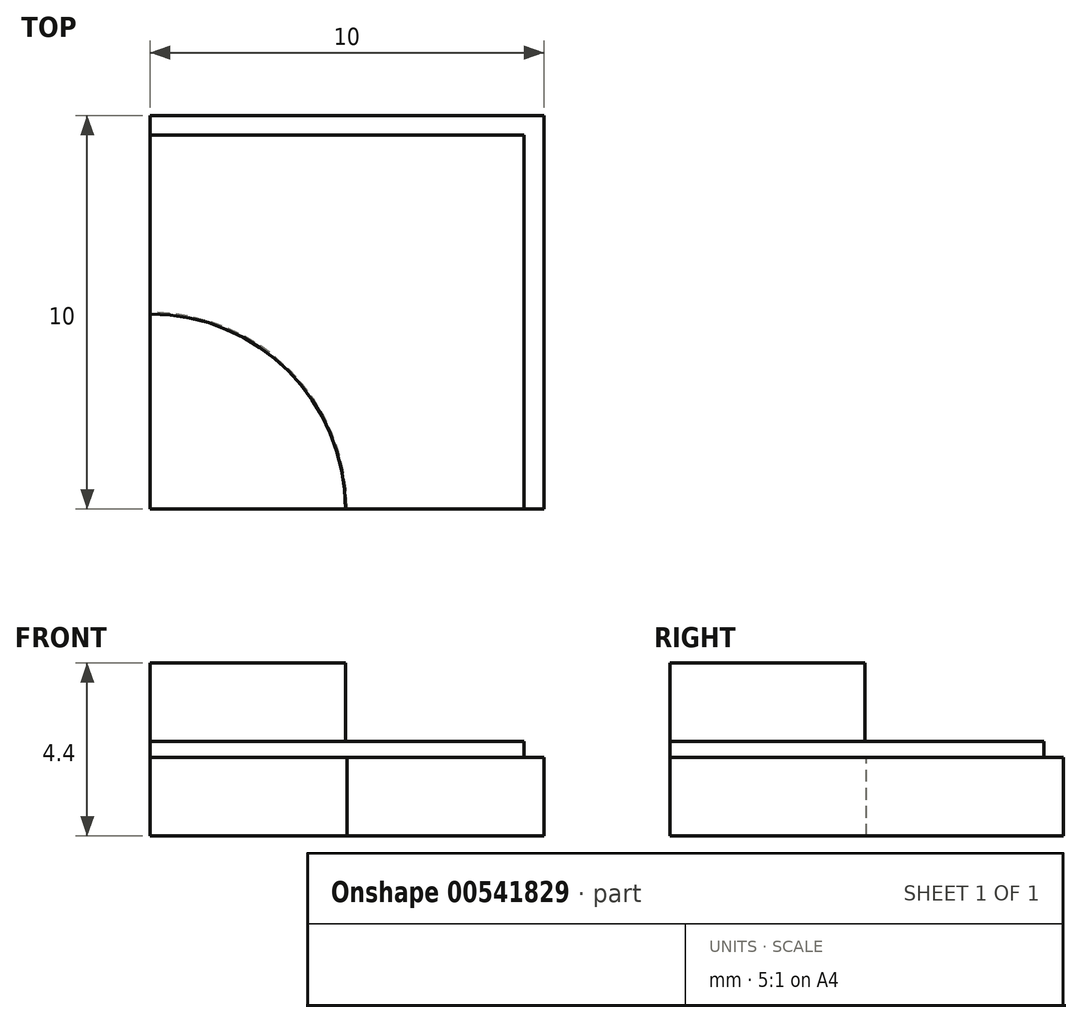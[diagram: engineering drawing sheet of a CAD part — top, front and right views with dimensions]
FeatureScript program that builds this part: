
annotation { "Feature Type Name" : "Feature", "Feature Type Description" : "" }
export const myFeature = defineFeature(function(context is Context, id is Id, definition is map)
    precondition{}
    {
        {
            var Q0;
            Q0=qCreatedBy(makeId("Top.planeOp"),FACE);
            var sketch = newSketch(context, id + "F0", { "sketchPlane" : qUnion([Q0])});
            skLineSegment(sketch, "E0.bottom", {"start": v(0, 0) * mm, "end": v(10, 0) * mm, "construction": true});
            skLineSegment(sketch, "E0.top", {"start": v(0, 10) * mm, "end": v(10, 10) * mm, "construction": true});
            skLineSegment(sketch, "E0.left", {"start": v(0, 0) * mm, "end": v(0, 10) * mm, "construction": true});
            skLineSegment(sketch, "E0.right", {"start": v(10, 0) * mm, "end": v(10, 10) * mm, "construction": true});
            skCircle(sketch, "E1", {"center": v(0, 0) * mm, "radius": 5 * mm, "construction": true});
            skArc(sketch, "E2", {"start": v(5, 0) * mm, "mid": v(3.54, 3.54) * mm, "end": v(0, 5) * mm});
            skLineSegment(sketch, "E3", {"start": v(0, 5) * mm, "end": v(0, 10) * mm});
            skLineSegment(sketch, "E4", {"start": v(10, 10) * mm, "end": v(10, 0) * mm});
            skLineSegment(sketch, "E5", {"start": v(5, 0) * mm, "end": v(10, 0) * mm});
            skLineSegment(sketch, "E6", {"start": v(10, 10) * mm, "end": v(0, 10) * mm});
            skSolve(sketch);
        }
        {
            var Q0;
            Q0=makeQuery(id+"F0.imprint","IMPRINT",FACE,{"disambiguationData":[TD([[makeQuery(id+"F0.imprint","IMPRINT",EDGE,{"derivedFrom":sQuery(id+"F0.wireOp",EDGE,"E2")}),-1.0]])]});
            extrude(context, id + "F1", {"entities" : qUnion([Q0]), "oppositeDirection" : true, "depth" : 2 * mm, "offsetDistance" : 25 * mm});
        }
        {
            var Q0;
            Q0=makeQuery(id+"F1.opExtrude","CAP_FACE",FACE,{"disambiguationData":[OSD([sQuery(id+"F0.wireOp",EDGE,"E2"),sQuery(id+"F0.wireOp",EDGE,"E3"),sQuery(id+"F0.wireOp",EDGE,"E4"),sQuery(id+"F0.wireOp",EDGE,"E5"),sQuery(id+"F0.wireOp",EDGE,"E6")])],"isStart":true});
            var sketch = newSketch(context, id + "F2", { "sketchPlane" : qUnion([Q0])});
            skLineSegment(sketch, "E7.0.0", {"start": v(10, 0) * mm, "end": v(10, 10) * mm, "construction": true});
            skLineSegment(sketch, "E7.0.1", {"start": v(10, 10) * mm, "end": v(0, 10) * mm, "construction": true});
            skLineSegment(sketch, "E7.0.2", {"start": v(0, 10) * mm, "end": v(0, 5) * mm, "construction": true});
            skArc(sketch, "E7.0.3", {"start": v(0, 5) * mm, "mid": v(3.54, 3.54) * mm, "end": v(5, 0) * mm, "construction": true});
            skLineSegment(sketch, "E7.0.4", {"start": v(5, 0) * mm, "end": v(10, 0) * mm, "construction": true});
            skLineSegment(sketch, "E8.bottom", {"start": v(0, 0) * mm, "end": v(9.5, 0) * mm});
            skLineSegment(sketch, "E8.top", {"start": v(0, 9.5) * mm, "end": v(9.5, 9.5) * mm});
            skLineSegment(sketch, "E8.left", {"start": v(0, 0) * mm, "end": v(0, 9.5) * mm});
            skLineSegment(sketch, "E8.right", {"start": v(9.5, 0) * mm, "end": v(9.5, 9.5) * mm});
            skSolve(sketch);
        }
        {
            var Q0;
            {var subQ1=makeQuery(id+"F1.opExtrude","CAP_EDGE",EDGE,{"disambiguationData":[OSD([sQuery(id+"F0.wireOp",EDGE,"E2")])],"isStart":true});Q0=makeQuery(id+"F2.imprint","IMPRINT",FACE,{"disambiguationData":[TD([[makeQuery(id+"F2.imprint","IMPRINT",EDGE,{"derivedFrom":subQ1}),1.0]])]});}
            var Q1;
            {var subQ3=sQuery(id+"F2.wireOp",EDGE,"E8.top");Q1=makeQuery(id+"F2.imprint","IMPRINT",FACE,{"disambiguationData":[TD([[makeQuery(id+"F2.imprint","IMPRINT",EDGE,{"derivedFrom":subQ3}),-1.0]])]});}
            extrude(context, id + "F3", {"entities" : qUnion([Q0, Q1]), "depth" : 0.4 * mm, "offsetDistance" : 25 * mm});
        }
        {
            var Q0;
            Q0=makeQuery(id+"F3.opExtrude","CAP_FACE",FACE,{"disambiguationData":[OSD([sQuery(id+"F2.wireOp",EDGE,"E8.bottom"),sQuery(id+"F2.wireOp",EDGE,"E8.top"),sQuery(id+"F2.wireOp",EDGE,"E8.left"),sQuery(id+"F2.wireOp",EDGE,"E8.right")])],"isStart":false});
            var sketch = newSketch(context, id + "F4", { "sketchPlane" : qUnion([Q0])});
            skArc(sketch, "E9", {"start": v(4.96, 0) * mm, "mid": v(3.5, 3.5) * mm, "end": v(0, 4.96) * mm});
            skLineSegment(sketch, "E10", {"start": v(0, 4.96) * mm, "end": v(0, 0) * mm});
            skLineSegment(sketch, "E11", {"start": v(4.96, 0) * mm, "end": v(0, 0) * mm});
            skSolve(sketch);
        }
        {
            var Q0;
            Q0 = qSketchRegion(id + "F4", true);
            extrude(context, id + "F5", {"entities" : qUnion([Q0]), "depth" : 2 * mm, "offsetDistance" : 25 * mm});
        }
    });
